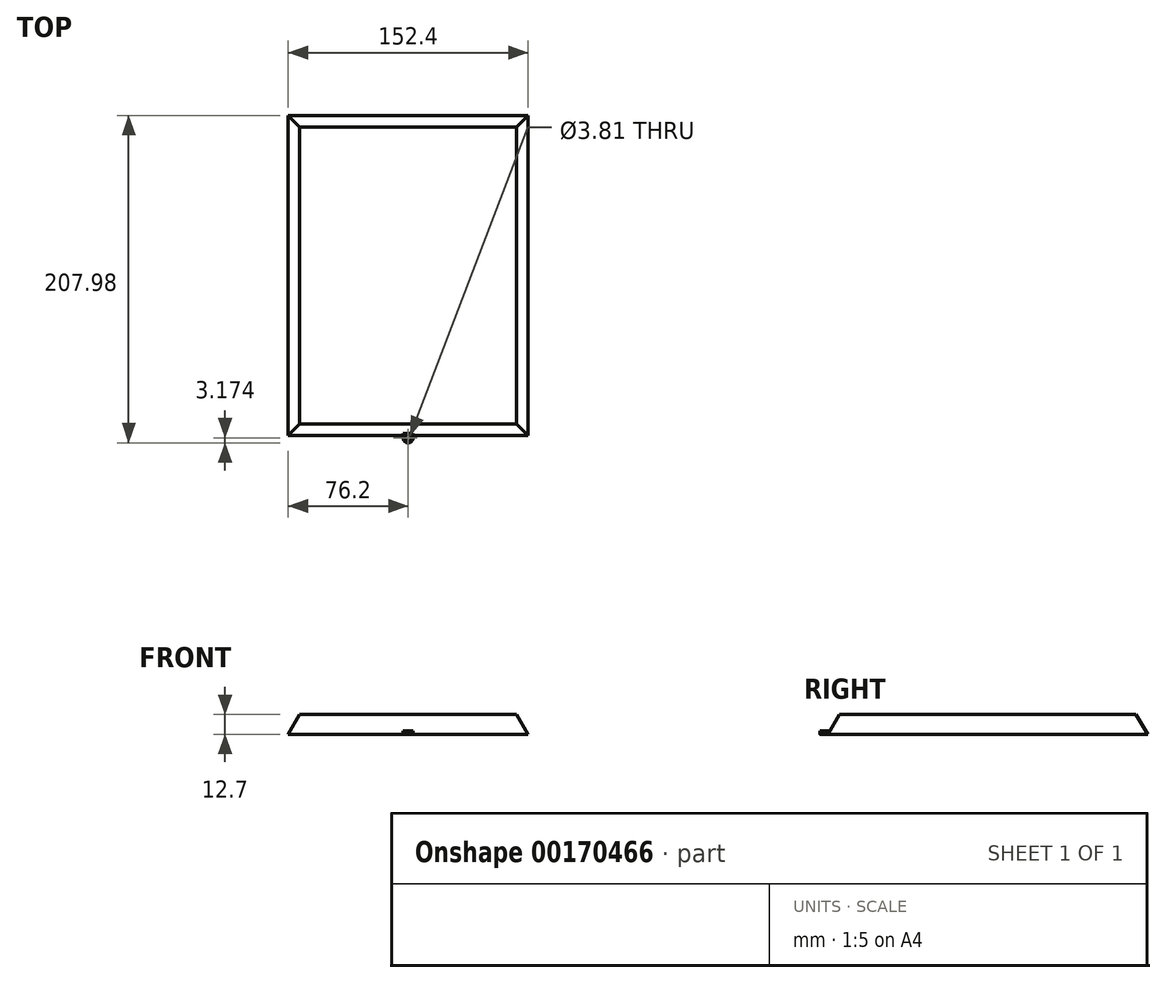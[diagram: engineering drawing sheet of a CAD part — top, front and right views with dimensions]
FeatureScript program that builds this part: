
annotation { "Feature Type Name" : "Feature", "Feature Type Description" : "" }
export const myFeature = defineFeature(function(context is Context, id is Id, definition is map)
    precondition{}
    {
        {
            var Q0;
            Q0=qCreatedBy(makeId("Top.planeOp"),FACE);
            var sketch = newSketch(context, id + "F0", { "sketchPlane" : qUnion([Q0])});
            skLineSegment(sketch, "E0.bottom", {"start": v(76.2, -101.6) * mm, "end": v(-76.2, -101.6) * mm});
            skLineSegment(sketch, "E0.top", {"start": v(76.2, 101.6) * mm, "end": v(-76.2, 101.6) * mm});
            skLineSegment(sketch, "E0.left", {"start": v(76.2, -101.6) * mm, "end": v(76.2, 101.6) * mm});
            skLineSegment(sketch, "E0.right", {"start": v(-76.2, -101.6) * mm, "end": v(-76.2, 101.6) * mm});
            skPoint(sketch, "E0.middle", {"position": v(0, 0) * mm});
            skSolve(sketch);
        }
        {
            var Q0;
            Q0=makeQuery(id+"F0.imprint","IMPRINT",FACE,{"disambiguationData":[TD([[makeQuery(id+"F0.imprint","IMPRINT",EDGE,{"derivedFrom":sQuery(id+"F0.wireOp",EDGE,"E0.bottom")}),-1.0]])]});
            extrude(context, id + "F1", {"entities" : qUnion([Q0]), "depth" : 12.7 * mm, "hasDraft" : true, "draftAngle" : 30 * degree, "draftPullDirection" : true});
        }
        {
            var Q0;
            Q0=makeQuery(id+"F1.opExtrude","CAP_FACE",FACE,{"disambiguationData":[OSD([sQuery(id+"F0.wireOp",EDGE,"E0.bottom"),sQuery(id+"F0.wireOp",EDGE,"E0.top"),sQuery(id+"F0.wireOp",EDGE,"E0.left"),sQuery(id+"F0.wireOp",EDGE,"E0.right")])],"isStart":true});
            var sketch = newSketch(context, id + "F2", { "sketchPlane" : qUnion([Q0])});
            skLineSegment(sketch, "E1.bottom", {"start": v(3.18, 100.03) * mm, "end": v(-3.18, 100.03) * mm});
            skLineSegment(sketch, "E1.left", {"start": v(3.17, 100.03) * mm, "end": v(3.17, 103.2) * mm});
            skLineSegment(sketch, "E1.right", {"start": v(-3.18, 100.03) * mm, "end": v(-3.18, 103.2) * mm});
            skPoint(sketch, "E1.middle", {"position": v(0, 101.62) * mm});
            skArc(sketch, "E2", {"start": v(3.18, 103.2) * mm, "mid": v(0, 106.38) * mm, "end": v(-3.17, 103.2) * mm});
            skPoint(sketch, "E3", {"position": v(0, 101.6) * mm});
            skSolve(sketch);
        }
        {
            var Q0;
            {var subQ0=sQuery(id+"F2.wireOp",EDGE,"E2");Q0=makeQuery(id+"F2.imprint","IMPRINT",FACE,{"disambiguationData":[TD([[makeQuery(id+"F2.imprint","IMPRINT",EDGE,{"derivedFrom":subQ0}),1.0]])]});}
            var Q1;
            {var subQ0=sQuery(id+"F2.wireOp",EDGE,"E1.bottom");Q1=makeQuery(id+"F2.imprint","IMPRINT",FACE,{"disambiguationData":[TD([[makeQuery(id+"F2.imprint","IMPRINT",EDGE,{"derivedFrom":subQ0}),-1.0]])]});}
            extrude(context, id + "F3", {"entities" : qUnion([Q0, Q1]), "operationType" : NewBodyOperationType.ADD, "oppositeDirection" : true, "depth" : 2.31 * mm});
        }
        {
            var Q0;
            Q0=makeQuery(id+"F3.opExtrude","CAP_FACE",FACE,{"disambiguationData":[OSD([sQuery(id+"F2.wireOp",EDGE,"E1.bottom"),sQuery(id+"F2.wireOp",EDGE,"E1.left"),sQuery(id+"F2.wireOp",EDGE,"E1.right"),sQuery(id+"F2.wireOp",EDGE,"E2")])],"isStart":false});
            var sketch = newSketch(context, id + "F4", { "sketchPlane" : qUnion([Q0])});
            skCircle(sketch, "E4", {"center": v(0, -103.2) * mm, "radius": 1.9 * mm});
            skSolve(sketch);
        }
        {
            var Q0;
            Q0=makeQuery(id+"F4.imprint","IMPRINT",FACE,{"disambiguationData":[TD([[makeQuery(id+"F4.imprint","IMPRINT",EDGE,{"derivedFrom":sQuery(id+"F4.wireOp",EDGE,"E4")}),1.0]])]});
            extrude(context, id + "F5", {"entities" : qUnion([Q0]), "operationType" : NewBodyOperationType.REMOVE, "oppositeDirection" : true, "depth" : 25.4 * mm});
        }
    });
